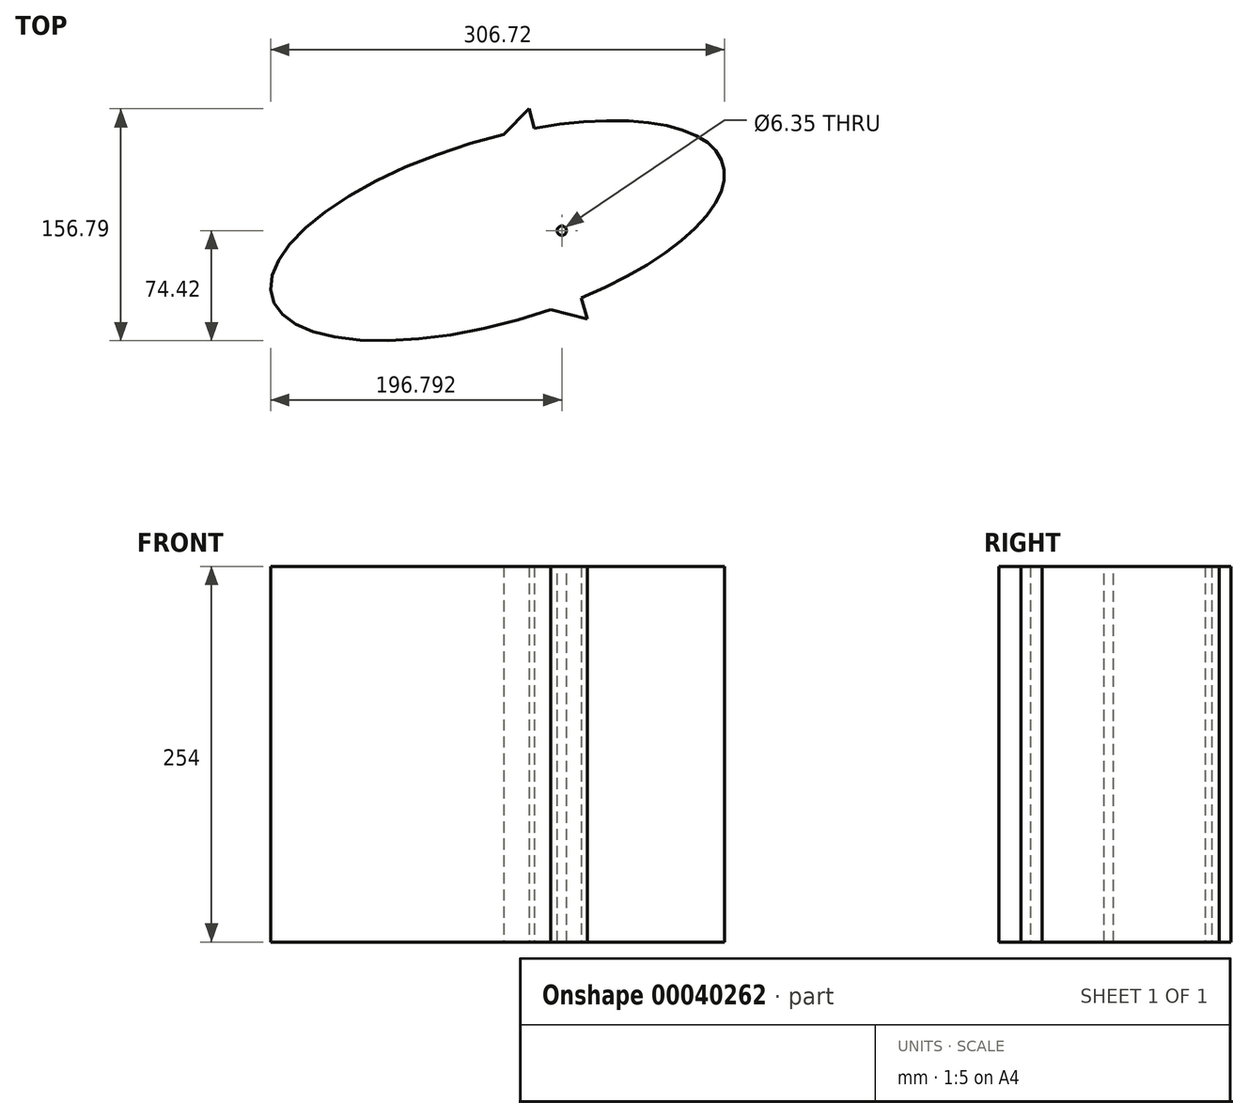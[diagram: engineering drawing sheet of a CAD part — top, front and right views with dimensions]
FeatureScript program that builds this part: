
annotation { "Feature Type Name" : "Feature", "Feature Type Description" : "" }
export const myFeature = defineFeature(function(context is Context, id is Id, definition is map)
    precondition{}
    {
        {
            var Q0;
            Q0=qCreatedBy(makeId("Top.planeOp"),FACE);
            var sketch = newSketch(context, id + "F0", { "sketchPlane" : qUnion([Q0])});
            skEllipse(sketch, "E0", {"center": v(0, 0) * mm, "majorRadius": 158.9 * mm, "minorRadius": 61.73 * mm, "majorAxis": v(0.96, 0.28)});
            skCircle(sketch, "E1.cCircle", {"center": v(0, 0) * mm, "radius": 42.54 * mm, "construction": true});
            skLineSegment(sketch, "E1.0", {"start": v(21.29, 82.37) * mm, "end": v(60.69, -59.62) * mm});
            skLineSegment(sketch, "E1.1", {"start": v(60.69, -59.62) * mm, "end": v(-81.98, -22.75) * mm});
            skLineSegment(sketch, "E1.2", {"start": v(-81.98, -22.75) * mm, "end": v(21.29, 82.37) * mm});
            skPoint(sketch, "E1.0.midPoint", {"position": v(40.99, 11.37) * mm});
            skSolve(sketch);
        }
        {
            var Q0;
            Q0 = qSketchRegion(id + "F0", true);
            extrude(context, id + "F1", {"entities" : qUnion([Q0]), "depth" : 254 * mm});
        }
        {
            var Q0;
            Q0 = qSketchRegion(id + "F0", true);
            var sketch = newSketch(context, id + "F2", { "sketchPlane" : qUnion([Q0])});
            skSolve(sketch);
        }
        {
            var Q0;
            Q0=makeQuery(id+"F1.opExtrude","CAP_FACE",FACE,{"disambiguationData":[OSD([sQuery(id+"F0.wireOp",EDGE,"E0"),sQuery(id+"F0.wireOp",EDGE,"E1.0"),sQuery(id+"F0.wireOp",EDGE,"E1.1"),sQuery(id+"F0.wireOp",EDGE,"E1.2")])],"isStart":false});
            var sketch = newSketch(context, id + "F3", { "sketchPlane" : qUnion([Q0])});
            skCircle(sketch, "E2", {"center": v(43.43, 0) * mm, "radius": 31.6 * mm});
            skSolve(sketch);
        }
        {
            var Q0;
            Q0=sQuery(id+"F3.wireOp",VERTEX,"E2.center");
            var Q1;
            Q1=makeQuery(id+"F1.opExtrude","SWEPT_BODY",BODY,{"disambiguationData":[OSD([sQuery(id+"F0.wireOp",EDGE,"E0"),sQuery(id+"F0.wireOp",EDGE,"E1.0"),sQuery(id+"F0.wireOp",EDGE,"E1.1"),sQuery(id+"F0.wireOp",EDGE,"E1.2")])]});
            hole(context, id + "F8", {"style" : HoleStyle.SIMPLE, "holeDiameter" : 6.35 * mm, "endStyle" : HoleEndStyle.THROUGH, "locations" : qUnion([Q0]), "scope" : qUnion([Q1])});
        }
    });
